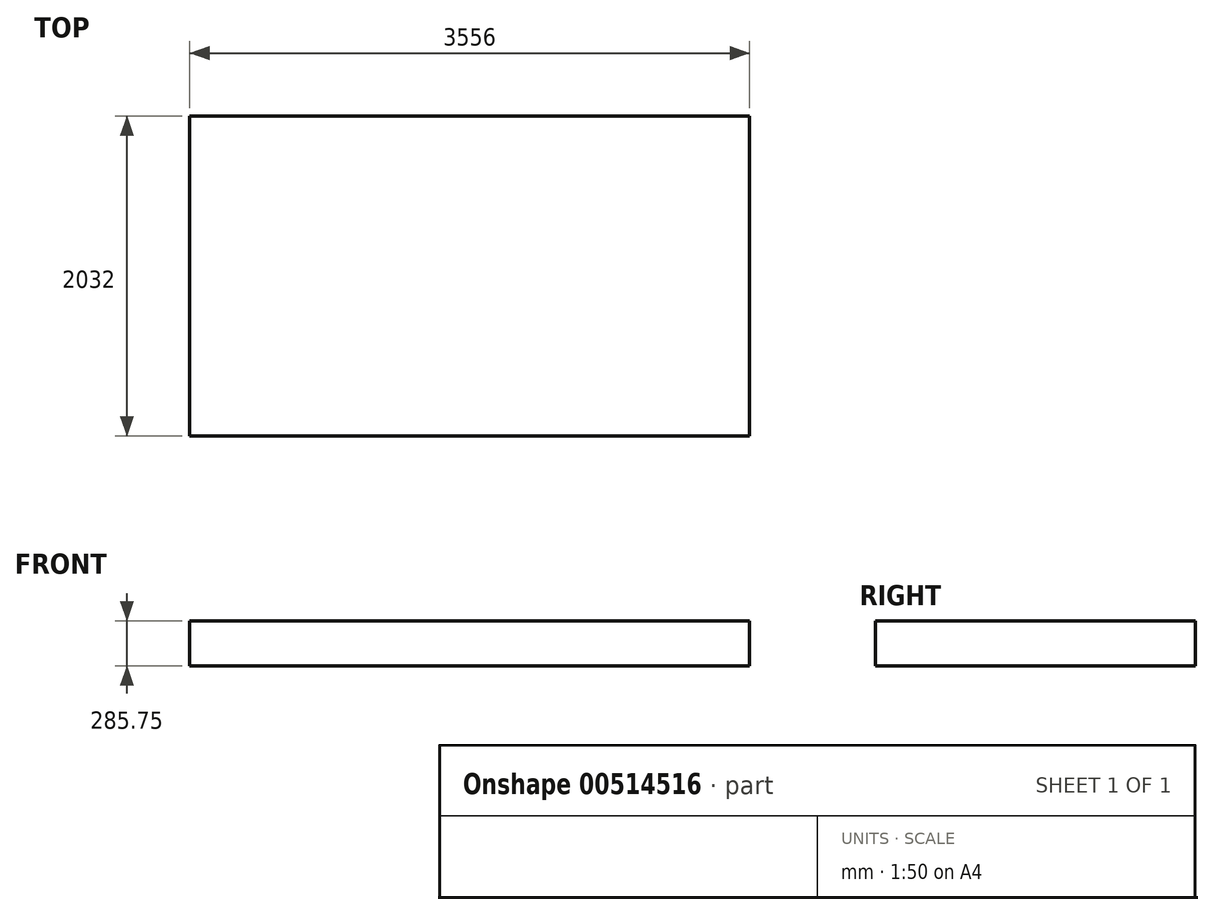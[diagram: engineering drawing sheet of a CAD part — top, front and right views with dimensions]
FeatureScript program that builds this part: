
annotation { "Feature Type Name" : "Feature", "Feature Type Description" : "" }
export const myFeature = defineFeature(function(context is Context, id is Id, definition is map)
    precondition{}
    {
        {
            var Q0;
            Q0=qCreatedBy(makeId("Top.planeOp"),FACE);
            var sketch = newSketch(context, id + "F0", { "sketchPlane" : qUnion([Q0])});
            skLineSegment(sketch, "E0.bottom", {"start": v(1778, 1016) * mm, "end": v(-1778, 1016) * mm});
            skLineSegment(sketch, "E0.top", {"start": v(1778, -1016) * mm, "end": v(-1778, -1016) * mm});
            skLineSegment(sketch, "E0.left", {"start": v(1778, 1016) * mm, "end": v(1778, -1016) * mm});
            skLineSegment(sketch, "E0.right", {"start": v(-1778, 1016) * mm, "end": v(-1778, -1016) * mm});
            skPoint(sketch, "E0.middle", {"position": v(0, 0) * mm});
            skSolve(sketch);
        }
        {
            var Q0;
            Q0=makeQuery(id+"F0.imprint","IMPRINT",FACE,{"disambiguationData":[TD([[makeQuery(id+"F0.imprint","IMPRINT",EDGE,{"derivedFrom":sQuery(id+"F0.wireOp",EDGE,"E0.bottom")}),1.0]])]});
            extrude(context, id + "F1", {"entities" : qUnion([Q0]), "depth" : 285.75 * mm, "offsetDistance" : 25.4 * mm});
        }
    });
